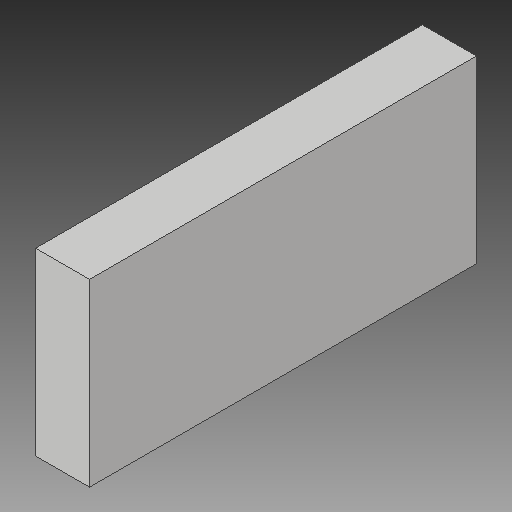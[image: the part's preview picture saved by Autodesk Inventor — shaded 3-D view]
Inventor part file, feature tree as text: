
AUTODESK INVENTOR PART (.ipt)
format: ipt  version: 2018 (Build 220112000, 112)  size: 116,224 bytes
history: native  units: mm
features: thread x4, extrude x3, sketch x3
ambient origin geometry x8: Origin, YZ Plane, XZ Plane, XY Plane, X Axis, Y Axis, Z Axis, Center Point
bodies: Solid1 (feature_tree)
feature tree (10):
  extrude  "Extrusion1"  Depth=86.0mm
  extrude  "Extrusion2"  Depth=12.0mm
  extrude  "Extrusion3"  Depth=10.0mm
  thread  "Thread1"  [1 undecoded]
  thread  "Thread2"  [1 undecoded]
  thread  "Thread3"  [1 undecoded]
  thread  "Thread4"  [1 undecoded]
  sketch  "Sketch1"  dims[d0=40.0mm d1=86.0mm]
  sketch  "Sketch2"  dims[d2=12.0mm d3=0.0mm d4=6.0mm]
  sketch  "Sketch3"  dims[d6=10.0mm d7=20.0mm d8=15.0mm d9=0.0mm d10=6.0mm d11=10.0mm d12=20.0mm d13=15.0mm d14=0.0mm d15=10.0mm d16=0.0mm d17=10.0mm d18=0.0mm d19=10.0mm d20=0.0mm d21=10.0mm d22=0.0mm]
note: 4 required parameter values undecoded (feature->parameter linkage not recoverable at this tier; creation-order binding heuristic only, values carry confidence <= 0.55)
